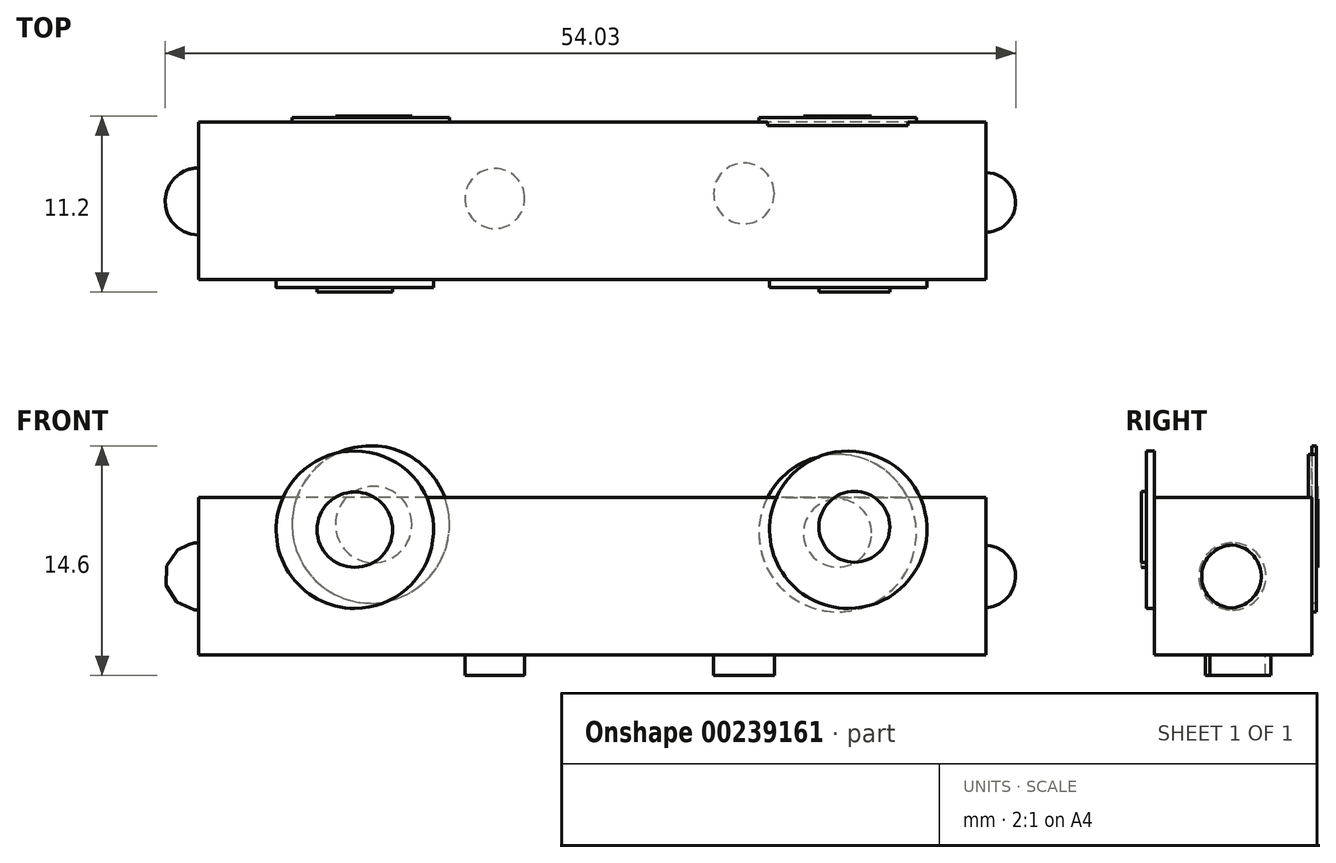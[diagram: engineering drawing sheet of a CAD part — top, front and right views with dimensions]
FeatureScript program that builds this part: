
annotation { "Feature Type Name" : "Feature", "Feature Type Description" : "" }
export const myFeature = defineFeature(function(context is Context, id is Id, definition is map)
    precondition{}
    {
        {
            var Q0;
            Q0=qCreatedBy(makeId("Front.planeOp"),FACE);
            var sketch = newSketch(context, id + "F0", { "sketchPlane" : qUnion([Q0])});
            skLineSegment(sketch, "E0.bottom", {"start": v(25, 5) * mm, "end": v(-25, 5) * mm});
            skLineSegment(sketch, "E0.top", {"start": v(25, -5) * mm, "end": v(-25, -5) * mm});
            skLineSegment(sketch, "E0.left", {"start": v(25, 5) * mm, "end": v(25, -5) * mm});
            skLineSegment(sketch, "E0.right", {"start": v(-25, 5) * mm, "end": v(-25, -5) * mm});
            skPoint(sketch, "E0.middle", {"position": v(0, 0) * mm});
            skSolve(sketch);
        }
        {
            var Q0;
            Q0 = qSketchRegion(id + "F0", true);
            extrude(context, id + "F1", {"entities" : qUnion([Q0]), "depth" : 10 * mm});
        }
        {
            var Q0;
            Q0=makeQuery(id+"F1.opExtrude","SWEPT_FACE",FACE,{"disambiguationData":[OSD([sQuery(id+"F0.wireOp",EDGE,"E0.right")])]});
            var sketch = newSketch(context, id + "F2", { "sketchPlane" : qUnion([Q0])});
            skArc(sketch, "E1", {"start": v(5.03, 2.13) * mm, "mid": v(2.9, 0) * mm, "end": v(5.03, -2.13) * mm});
            skLineSegment(sketch, "E2", {"start": v(5.03, -2.13) * mm, "end": v(5.03, 2.13) * mm});
            skSolve(sketch);
        }
        {
            var Q0;
            Q0=makeQuery(id+"F2.imprint","IMPRINT",FACE,{"disambiguationData":[TD([[makeQuery(id+"F2.imprint","IMPRINT",EDGE,{"derivedFrom":sQuery(id+"F2.wireOp",EDGE,"E1")}),1.0]])]});
            var Q1;
            Q1=sQuery(id+"F2.wireOp",EDGE,"E2");
            revolve(context, id + "F3", {"operationType" : NewBodyOperationType.ADD, "entities" : qUnion([Q0]), "axis" : qUnion([Q1]), "revolveType" : RevolveType.FULL});
        }
        {
            var Q0;
            Q0=makeQuery(id+"F1.opExtrude","SWEPT_FACE",FACE,{"disambiguationData":[OSD([sQuery(id+"F0.wireOp",EDGE,"E0.left")])]});
            var sketch = newSketch(context, id + "F4", { "sketchPlane" : qUnion([Q0])});
            skArc(sketch, "E3", {"start": v(-5.2, -2) * mm, "mid": v(-3.2, -0.1) * mm, "end": v(-4.99, 1.99) * mm});
            skLineSegment(sketch, "E4", {"start": v(-4.99, 1.99) * mm, "end": v(-5.2, -2) * mm});
            skSolve(sketch);
        }
        {
            var Q0;
            Q0=makeQuery(id+"F4.imprint","IMPRINT",FACE,{"disambiguationData":[TD([[makeQuery(id+"F4.imprint","IMPRINT",EDGE,{"derivedFrom":sQuery(id+"F4.wireOp",EDGE,"E3")}),1.0]])]});
            var Q1;
            Q1=sQuery(id+"F4.wireOp",EDGE,"E4");
            revolve(context, id + "F5", {"operationType" : NewBodyOperationType.ADD, "entities" : qUnion([Q0]), "axis" : qUnion([Q1]), "revolveType" : RevolveType.FULL});
        }
        {
            var Q0;
            Q0=makeQuery(id+"F1.opExtrude","SWEPT_FACE",FACE,{"disambiguationData":[OSD([sQuery(id+"F0.wireOp",EDGE,"E0.top")])]});
            var sketch = newSketch(context, id + "F6", { "sketchPlane" : qUnion([Q0])});
            skCircle(sketch, "E5", {"center": v(9.64, 4.53) * mm, "radius": 1.93 * mm});
            skCircle(sketch, "E6", {"center": v(-6.18, 4.85) * mm, "radius": 1.9 * mm});
            skSolve(sketch);
        }
        {
            var Q0;
            Q0 = qSketchRegion(id + "F6", true);
            extrude(context, id + "F7", {"entities" : qUnion([Q0]), "operationType" : NewBodyOperationType.ADD, "depth" : 1.3 * mm});
        }
        {
            var Q0;
            Q0=makeQuery(id+"F1.opExtrude","CAP_FACE",FACE,{"disambiguationData":[OSD([sQuery(id+"F0.wireOp",EDGE,"E0.bottom"),sQuery(id+"F0.wireOp",EDGE,"E0.top"),sQuery(id+"F0.wireOp",EDGE,"E0.left"),sQuery(id+"F0.wireOp",EDGE,"E0.right")])],"isStart":true});
            var sketch = newSketch(context, id + "F8", { "sketchPlane" : qUnion([Q0])});
            skCircle(sketch, "E7", {"center": v(-15.59, 2.75) * mm, "radius": 5 * mm});
            skCircle(sketch, "E8", {"center": v(14.06, 3.3) * mm, "radius": 5 * mm});
            skSolve(sketch);
        }
        {
            var Q0;
            Q0 = qSketchRegion(id + "F8", true);
            extrude(context, id + "F9", {"entities" : qUnion([Q0]), "operationType" : NewBodyOperationType.ADD, "depth" : 0.3 * mm});
        }
        {
            var Q0;
            Q0=makeQuery(id+"F9.opExtrude","CAP_FACE",FACE,{"disambiguationData":[OSD([sQuery(id+"F8.wireOp",EDGE,"E7")])],"isStart":false});
            var sketch = newSketch(context, id + "F10", { "sketchPlane" : qUnion([Q0])});
            skCircle(sketch, "E9", {"center": v(-15.59, 2.75) * mm, "radius": 2.16 * mm});
            skCircle(sketch, "E10", {"center": v(13.88, 3.3) * mm, "radius": 2.43 * mm});
            skSolve(sketch);
        }
        {
            var Q0;
            Q0 = qSketchRegion(id + "F10", true);
            extrude(context, id + "F11", {"entities" : qUnion([Q0]), "operationType" : NewBodyOperationType.ADD, "depth" : 0.1 * mm});
        }
        {
            var Q0;
            Q0=makeQuery(id+"F1.opExtrude","CAP_FACE",FACE,{"disambiguationData":[OSD([sQuery(id+"F0.wireOp",EDGE,"E0.bottom"),sQuery(id+"F0.wireOp",EDGE,"E0.top"),sQuery(id+"F0.wireOp",EDGE,"E0.left"),sQuery(id+"F0.wireOp",EDGE,"E0.right")])],"isStart":false});
            var sketch = newSketch(context, id + "F12", { "sketchPlane" : qUnion([Q0])});
            skCircle(sketch, "E11", {"center": v(-15.07, 2.97) * mm, "radius": 5 * mm});
            skCircle(sketch, "E12", {"center": v(16.27, 2.97) * mm, "radius": 5 * mm});
            skSolve(sketch);
        }
        {
            var Q0;
            Q0 = qSketchRegion(id + "F12", true);
            var Q1;
            Q1=makeQuery(id+"F9.opExtrude","CAP_FACE",FACE,{"disambiguationData":[OSD([sQuery(id+"F8.wireOp",EDGE,"E7")])],"isStart":false});
            extrude(context, id + "F13", {"entities" : qUnion([Q0, Q1]), "operationType" : NewBodyOperationType.ADD, "depth" : 0.5 * mm});
        }
        {
            var Q0;
            Q0=makeQuery(id+"F13.opExtrude","CAP_FACE",FACE,{"disambiguationData":[OSD([sQuery(id+"F12.wireOp",EDGE,"E11")])],"isStart":false});
            var sketch = newSketch(context, id + "F14", { "sketchPlane" : qUnion([Q0])});
            skCircle(sketch, "E13", {"center": v(-15.07, 2.97) * mm, "radius": 2.4 * mm});
            skCircle(sketch, "E14", {"center": v(16.66, 3.15) * mm, "radius": 2.25 * mm});
            skSolve(sketch);
        }
        {
            var Q0;
            Q0 = qSketchRegion(id + "F14", true);
            extrude(context, id + "F15", {"entities" : qUnion([Q0]), "operationType" : NewBodyOperationType.ADD, "depth" : 0.3 * mm});
        }
    });
